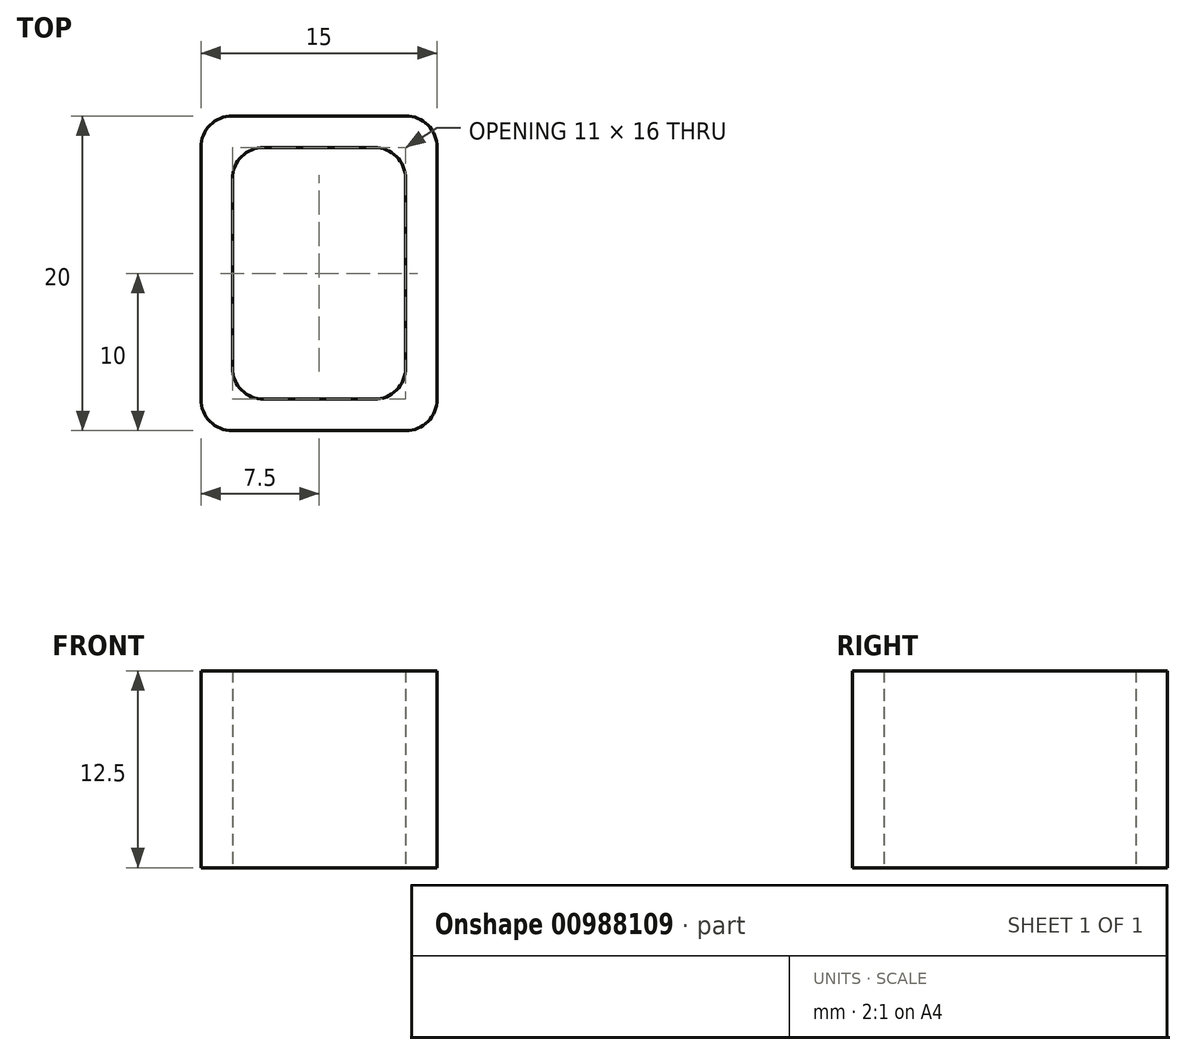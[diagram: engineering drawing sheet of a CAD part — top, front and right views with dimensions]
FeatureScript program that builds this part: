
annotation { "Feature Type Name" : "Feature", "Feature Type Description" : "" }
export const myFeature = defineFeature(function(context is Context, id is Id, definition is map)
    precondition{}
    {
        {
            var Q0;
            Q0=qCreatedBy(makeId("Top.planeOp"),FACE);
            var sketch = newSketch(context, id + "F0", { "sketchPlane" : qUnion([Q0])});
            skLineSegment(sketch, "E0", {"start": v(0, 0) * mm, "end": v(0, 20) * mm, "construction": true});
            skLineSegment(sketch, "E1", {"start": v(0, 20) * mm, "end": v(15, 20) * mm, "construction": true});
            skLineSegment(sketch, "E2", {"start": v(15, 20) * mm, "end": v(15, 0) * mm, "construction": true});
            skLineSegment(sketch, "E3.bottom", {"start": v(2, 0) * mm, "end": v(13, 0) * mm});
            skLineSegment(sketch, "E3.top", {"start": v(2, 20) * mm, "end": v(13, 20) * mm});
            skLineSegment(sketch, "E3.left", {"start": v(0, 2) * mm, "end": v(0, 18) * mm});
            skLineSegment(sketch, "E3.right", {"start": v(15, 2) * mm, "end": v(15, 18) * mm});
            skLineSegment(sketch, "E4.bottom", {"start": v(4, 18) * mm, "end": v(11, 18) * mm});
            skLineSegment(sketch, "E4.top", {"start": v(4, 2) * mm, "end": v(11, 2) * mm});
            skLineSegment(sketch, "E4.left", {"start": v(2, 16) * mm, "end": v(2, 4) * mm});
            skLineSegment(sketch, "E4.right", {"start": v(13, 16) * mm, "end": v(13, 4) * mm});
            skPoint(sketch, "E5.visualSharp", {"position": v(2, 18) * mm});
            skArc(sketch, "E5.filletArc", {"start": v(4, 18) * mm, "mid": v(2.59, 17.41) * mm, "end": v(2, 16) * mm});
            skPoint(sketch, "E6.visualSharp", {"position": v(13, 18) * mm});
            skArc(sketch, "E6.filletArc", {"start": v(13, 16) * mm, "mid": v(12.41, 17.41) * mm, "end": v(11, 18) * mm});
            skPoint(sketch, "E7.visualSharp", {"position": v(13, 2) * mm});
            skArc(sketch, "E7.filletArc", {"start": v(11, 2) * mm, "mid": v(12.41, 2.59) * mm, "end": v(13, 4) * mm});
            skPoint(sketch, "E8.visualSharp", {"position": v(2, 2) * mm});
            skArc(sketch, "E8.filletArc", {"start": v(2, 4) * mm, "mid": v(2.59, 2.59) * mm, "end": v(4, 2) * mm});
            skPoint(sketch, "E9.visualSharp", {"position": v(0, 0) * mm});
            skArc(sketch, "E9.filletArc", {"start": v(0, 2) * mm, "mid": v(0.59, 0.59) * mm, "end": v(2, 0) * mm});
            skPoint(sketch, "E10.visualSharp", {"position": v(15, 0) * mm});
            skArc(sketch, "E10.filletArc", {"start": v(13, 0) * mm, "mid": v(14.41, 0.59) * mm, "end": v(15, 2) * mm});
            skPoint(sketch, "E11.visualSharp", {"position": v(15, 20) * mm});
            skArc(sketch, "E11.filletArc", {"start": v(15, 18) * mm, "mid": v(14.41, 19.41) * mm, "end": v(13, 20) * mm});
            skPoint(sketch, "E12.visualSharp", {"position": v(0, 20) * mm});
            skArc(sketch, "E12.filletArc", {"start": v(2, 20) * mm, "mid": v(0.59, 19.41) * mm, "end": v(0, 18) * mm});
            skSolve(sketch);
        }
        {
            var Q0;
            Q0 = qSketchRegion(id + "F0", true);
            var Q1;
            Q1=makeQuery(id+"F0.imprint","IMPRINT",FACE,{"disambiguationData":[TD([[makeQuery(id+"F0.imprint","IMPRINT",EDGE,{"derivedFrom":sQuery(id+"F0.wireOp",EDGE,"E3.bottom")}),1.0]])]});
            extrude(context, id + "F1", {"entities" : qUnion([Q0, Q1]), "depth" : 12.5 * mm, "offsetDistance" : 25 * mm});
        }
    });
